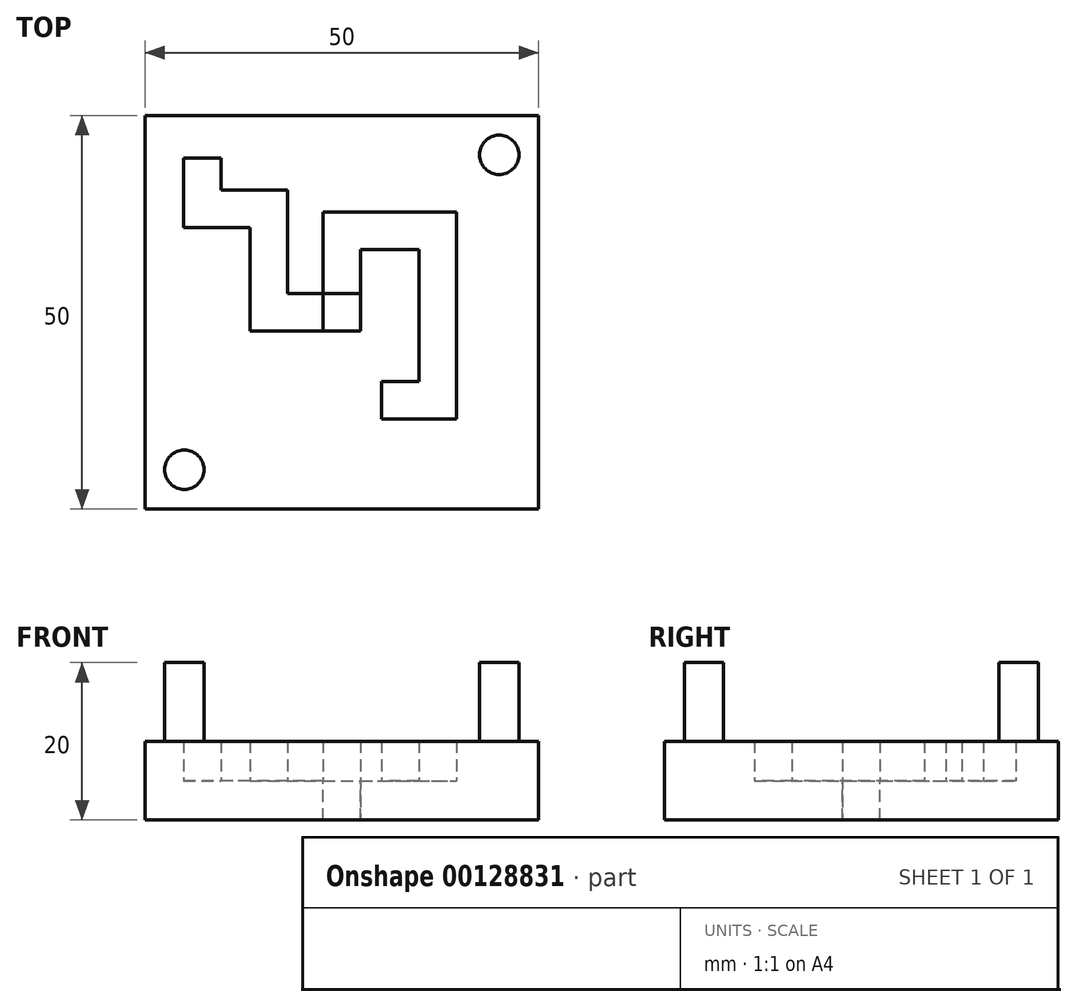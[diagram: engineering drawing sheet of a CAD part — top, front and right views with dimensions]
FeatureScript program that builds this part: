
annotation { "Feature Type Name" : "Feature", "Feature Type Description" : "" }
export const myFeature = defineFeature(function(context is Context, id is Id, definition is map)
    precondition{}
    {
        {
            var Q0;
            Q0=qCreatedBy(makeId("Top.planeOp"),FACE);
            var sketch = newSketch(context, id + "F0", { "sketchPlane" : qUnion([Q0])});
            skLineSegment(sketch, "E0.bottom", {"start": v(0, 0) * mm, "end": v(50, 0) * mm});
            skLineSegment(sketch, "E0.top", {"start": v(0, -50) * mm, "end": v(50, -50) * mm});
            skLineSegment(sketch, "E0.left", {"start": v(0, 0) * mm, "end": v(0, -50) * mm});
            skLineSegment(sketch, "E0.right", {"start": v(50, 0) * mm, "end": v(50, -50) * mm});
            skLineSegment(sketch, "E1", {"start": v(25, 0) * mm, "end": v(25, -50) * mm, "construction": true});
            skLineSegment(sketch, "E2", {"start": v(0, -25) * mm, "end": v(50, -25) * mm, "construction": true});
            skLineSegment(sketch, "E3", {"start": v(22.62, -25) * mm, "end": v(22.62, -22.62) * mm});
            skLineSegment(sketch, "E4", {"start": v(22.62, -22.62) * mm, "end": v(25, -22.62) * mm});
            skLineSegment(sketch, "E5", {"start": v(27.38, -22.62) * mm, "end": v(27.38, -25) * mm});
            skLineSegment(sketch, "E6", {"start": v(27.38, -25) * mm, "end": v(27.38, -27.38) * mm});
            skLineSegment(sketch, "E7", {"start": v(27.38, -27.38) * mm, "end": v(25, -27.38) * mm});
            skLineSegment(sketch, "E8", {"start": v(25, -27.38) * mm, "end": v(22.62, -27.38) * mm});
            skLineSegment(sketch, "E9", {"start": v(22.62, -27.38) * mm, "end": v(22.62, -25) * mm});
            skLineSegment(sketch, "E10", {"start": v(27.38, -22.62) * mm, "end": v(25, -22.62) * mm});
            skLineSegment(sketch, "E11", {"start": v(22.62, -22.62) * mm, "end": v(22.62, -12.24) * mm});
            skLineSegment(sketch, "E12", {"start": v(27.38, -22.62) * mm, "end": v(27.38, -17) * mm});
            skLineSegment(sketch, "E13", {"start": v(27.38, -17) * mm, "end": v(34.78, -17) * mm});
            skLineSegment(sketch, "E14", {"start": v(34.78, -17) * mm, "end": v(34.78, -33.8) * mm});
            skLineSegment(sketch, "E15", {"start": v(34.78, -33.8) * mm, "end": v(30.02, -33.8) * mm});
            skLineSegment(sketch, "E16", {"start": v(30.02, -33.8) * mm, "end": v(30.02, -38.56) * mm});
            skLineSegment(sketch, "E17", {"start": v(30.02, -38.56) * mm, "end": v(34.78, -38.56) * mm});
            skLineSegment(sketch, "E18", {"start": v(34.78, -38.56) * mm, "end": v(39.55, -38.56) * mm});
            skLineSegment(sketch, "E19", {"start": v(39.55, -38.56) * mm, "end": v(39.55, -17) * mm});
            skLineSegment(sketch, "E20", {"start": v(22.62, -12.24) * mm, "end": v(39.55, -12.24) * mm});
            skLineSegment(sketch, "E21", {"start": v(39.55, -12.24) * mm, "end": v(39.55, -17) * mm});
            skLineSegment(sketch, "E22", {"start": v(13.34, -27.38) * mm, "end": v(13.34, -14.24) * mm});
            skLineSegment(sketch, "E23", {"start": v(13.34, -14.24) * mm, "end": v(4.88, -14.24) * mm});
            skLineSegment(sketch, "E24", {"start": v(22.62, -22.62) * mm, "end": v(18.1, -22.62) * mm});
            skLineSegment(sketch, "E25", {"start": v(18.1, -22.62) * mm, "end": v(18.1, -14.24) * mm});
            skLineSegment(sketch, "E26", {"start": v(18.1, -14.24) * mm, "end": v(18.1, -9.47) * mm});
            skLineSegment(sketch, "E27", {"start": v(9.64, -9.47) * mm, "end": v(9.64, -5.4) * mm});
            skLineSegment(sketch, "E28", {"start": v(4.88, -5.4) * mm, "end": v(9.64, -5.4) * mm});
            skLineSegment(sketch, "E29", {"start": v(34.78, -38.56) * mm, "end": v(34.78, -33.8) * mm});
            skLineSegment(sketch, "E30", {"start": v(13.34, -27.38) * mm, "end": v(18.1, -27.38) * mm});
            skLineSegment(sketch, "E31", {"start": v(22.62, -27.38) * mm, "end": v(18.1, -27.38) * mm});
            skLineSegment(sketch, "E32", {"start": v(18.1, -9.47) * mm, "end": v(13.34, -9.47) * mm});
            skLineSegment(sketch, "E33", {"start": v(13.34, -9.47) * mm, "end": v(9.64, -9.47) * mm});
            skLineSegment(sketch, "E34", {"start": v(4.88, -14.24) * mm, "end": v(4.88, -9.47) * mm});
            skLineSegment(sketch, "E35", {"start": v(4.88, -5.4) * mm, "end": v(4.88, -9.47) * mm});
            skPoint(sketch, "E36.center.orphan", {"position": v(5, -25) * mm});
            skPoint(sketch, "E37.center.orphan", {"position": v(25, -45) * mm});
            skCircle(sketch, "E38", {"center": v(5, -45) * mm, "radius": 2.5 * mm});
            skCircle(sketch, "E39", {"center": v(45, -5) * mm, "radius": 2.5 * mm});
            skSolve(sketch);
        }
        {
            var Q0;
            Q0=makeQuery(id+"F0.imprint","IMPRINT",FACE,{"disambiguationData":[TD([[makeQuery(id+"F0.imprint","IMPRINT",EDGE,{"derivedFrom":sQuery(id+"F0.wireOp",EDGE,"E0.bottom")}),-1.0]])]});
            extrude(context, id + "F1", {"entities" : qUnion([Q0]), "endBound" : BoundingType.SYMMETRIC, "depth" : 10 * mm});
        }
        {
            var Q0;
            Q0=makeQuery(id+"F0.imprint","IMPRINT",FACE,{"disambiguationData":[TD([[makeQuery(id+"F0.imprint","IMPRINT",EDGE,{"derivedFrom":sQuery(id+"F0.wireOp",EDGE,"E3")}),1.0]])]});
            var Q1;
            Q1=makeQuery(id+"F0.imprint","IMPRINT",FACE,{"disambiguationData":[TD([[makeQuery(id+"F0.imprint","IMPRINT",EDGE,{"derivedFrom":sQuery(id+"F0.wireOp",EDGE,"E4")}),1.0]])]});
            var Q2;
            Q2=makeQuery(id+"F0.imprint","IMPRINT",FACE,{"disambiguationData":[TD([[makeQuery(id+"F0.imprint","IMPRINT",EDGE,{"derivedFrom":sQuery(id+"F0.wireOp",EDGE,"E15")}),1.0]])]});
            extrude(context, id + "F2", {"entities" : qUnion([Q0, Q1, Q2]), "operationType" : NewBodyOperationType.REMOVE, "depth" : 2.38 * mm});
        }
        {
            var Q0;
            Q0=makeQuery(id+"F0.imprint","IMPRINT",FACE,{"disambiguationData":[TD([[makeQuery(id+"F0.imprint","IMPRINT",EDGE,{"derivedFrom":sQuery(id+"F0.wireOp",EDGE,"E4")}),1.0]])]});
            var Q1;
            Q1=makeQuery(id+"F0.imprint","IMPRINT",FACE,{"disambiguationData":[TD([[makeQuery(id+"F0.imprint","IMPRINT",EDGE,{"derivedFrom":sQuery(id+"F0.wireOp",EDGE,"E15")}),1.0]])]});
            var Q2;
            Q2=makeQuery(id+"F0.imprint","IMPRINT",FACE,{"disambiguationData":[TD([[makeQuery(id+"F0.imprint","IMPRINT",EDGE,{"derivedFrom":sQuery(id+"F0.wireOp",EDGE,"E3")}),1.0]])]});
            extrude(context, id + "F3", {"entities" : qUnion([Q0, Q1, Q2]), "operationType" : NewBodyOperationType.ADD, "oppositeDirection" : true, "depth" : 5 * mm});
        }
        {
            var Q0;
            Q0=makeQuery(id+"F0.imprint","IMPRINT",FACE,{"disambiguationData":[TD([[makeQuery(id+"F0.imprint","IMPRINT",EDGE,{"derivedFrom":sQuery(id+"F0.wireOp",EDGE,"E38")}),1.0]])]});
            var Q1;
            Q1=makeQuery(id+"F0.imprint","IMPRINT",FACE,{"disambiguationData":[TD([[makeQuery(id+"F0.imprint","IMPRINT",EDGE,{"derivedFrom":sQuery(id+"F0.wireOp",EDGE,"E39")}),1.0]])]});
            extrude(context, id + "F4", {"entities" : qUnion([Q0, Q1]), "operationType" : NewBodyOperationType.ADD, "depth" : 15 * mm, "hasSecondDirection" : true, "secondDirectionOppositeDirection" : true, "secondDirectionDepth" : 5 * mm});
        }
    });
